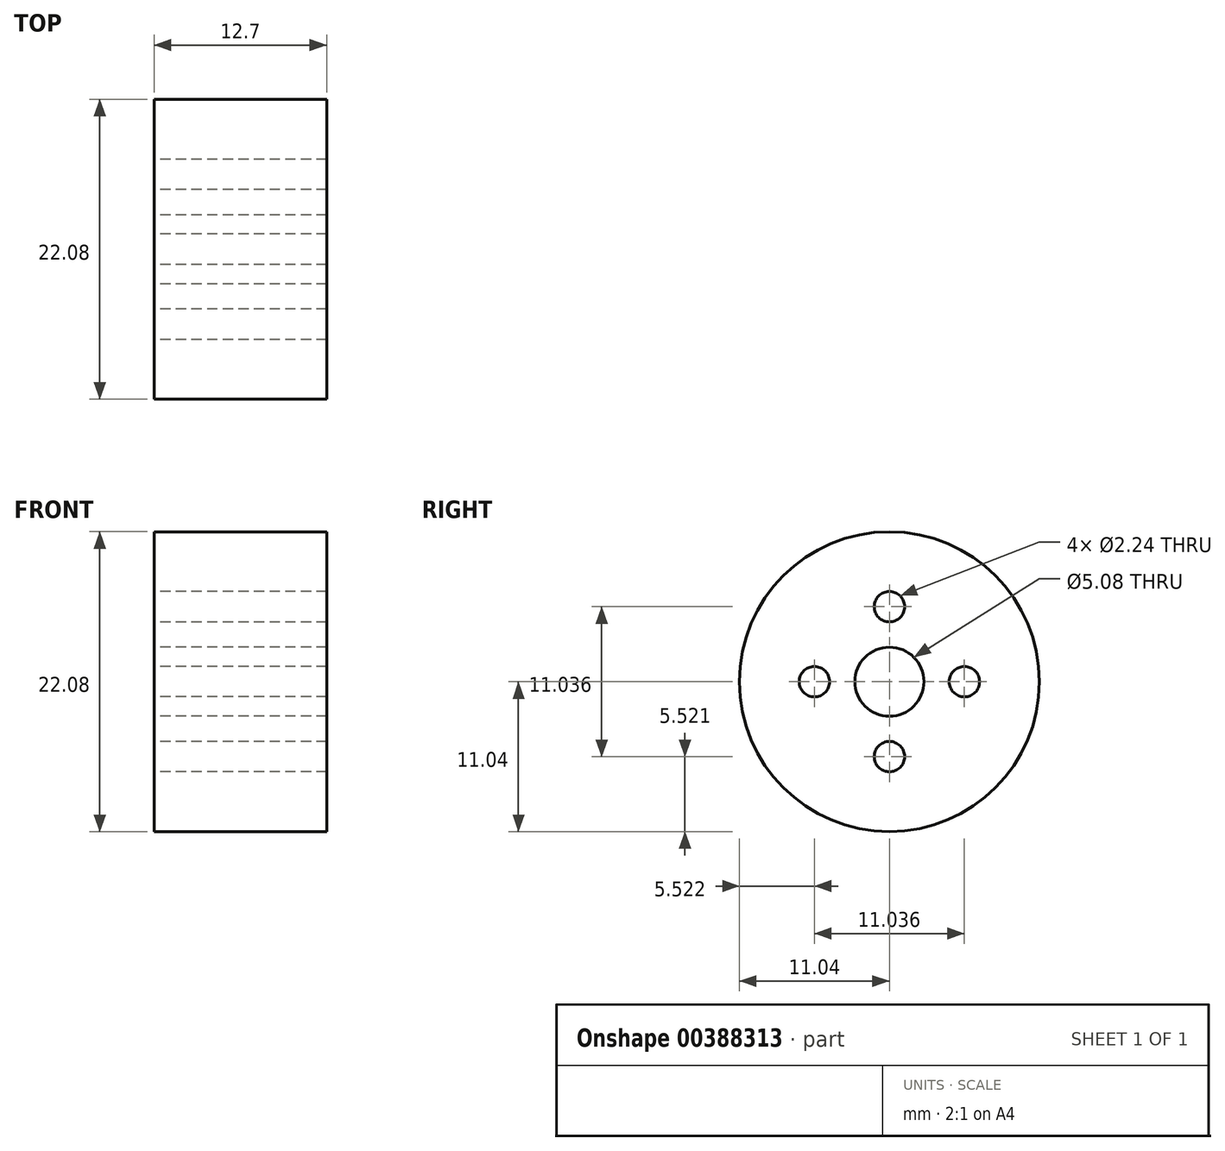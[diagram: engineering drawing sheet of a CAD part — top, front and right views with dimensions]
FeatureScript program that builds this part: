
annotation { "Feature Type Name" : "Feature", "Feature Type Description" : "" }
export const myFeature = defineFeature(function(context is Context, id is Id, definition is map)
    precondition{}
    {
        {
            var Q0;
            Q0=qCreatedBy(makeId("Front.planeOp"),FACE);
            var sketch = newSketch(context, id + "F0", { "sketchPlane" : qUnion([Q0])});
            skLineSegment(sketch, "E0", {"start": v(-13.23, 7.89) * mm, "end": v(-0.53, 7.89) * mm});
            skLineSegment(sketch, "E1", {"start": v(-0.53, 7.89) * mm, "end": v(-0.53, -3.15) * mm});
            skLineSegment(sketch, "E2", {"start": v(-0.53, -3.15) * mm, "end": v(-13.23, -3.15) * mm});
            skLineSegment(sketch, "E3", {"start": v(-13.23, -3.15) * mm, "end": v(-13.23, 7.89) * mm});
            skSolve(sketch);
        }
        {
            var Q0;
            Q0=qSketchRegion(id+"F0",true);
            var Q1;
            Q1=sQuery(id+"F0.wireOp",EDGE,"E2");
            revolve(context, id + "F1", {"entities" : qUnion([Q0]), "axis" : qUnion([Q1]), "revolveType" : RevolveType.FULL});
        }
        {
            var Q0;
            Q0=makeQuery(id+"F1.opRevolve","SWEPT_FACE",FACE,{"disambiguationData":[OSD([sQuery(id+"F0.wireOp",EDGE,"E3")])]});
            var sketch = newSketch(context, id + "F2", { "sketchPlane" : qUnion([Q0])});
            skCircle(sketch, "E4", {"center": v(0, -3.15) * mm, "radius": 2.54 * mm});
            skLineSegment(sketch, "E5", {"start": v(0, -3.15) * mm, "end": v(-11.04, -3.15) * mm, "construction": true});
            skLineSegment(sketch, "E6", {"start": v(0, -3.15) * mm, "end": v(0, 7.89) * mm, "construction": true});
            skLineSegment(sketch, "E7", {"start": v(0, 7.89) * mm, "end": v(0, -14.19) * mm, "construction": true});
            skLineSegment(sketch, "E8", {"start": v(0, -3.15) * mm, "end": v(11.04, -3.15) * mm, "construction": true});
            skCircle(sketch, "E9", {"center": v(-5.52, -3.15) * mm, "radius": 1.12 * mm});
            skCircle(sketch, "E10", {"center": v(0, 2.37) * mm, "radius": 1.12 * mm});
            skCircle(sketch, "E11", {"center": v(5.52, -3.15) * mm, "radius": 1.12 * mm});
            skLineSegment(sketch, "E12", {"start": v(0, -3.15) * mm, "end": v(0, -14.19) * mm, "construction": true});
            skCircle(sketch, "E13", {"center": v(0, -8.67) * mm, "radius": 1.12 * mm});
            skSolve(sketch);
        }
        {
            var Q0;
            Q0=qSketchRegion(id+"F2",true);
            extrude(context, id + "F3", {"entities" : qUnion([Q0]), "operationType" : NewBodyOperationType.REMOVE, "oppositeDirection" : true, "depth" : 30.43 * mm});
        }
    });
